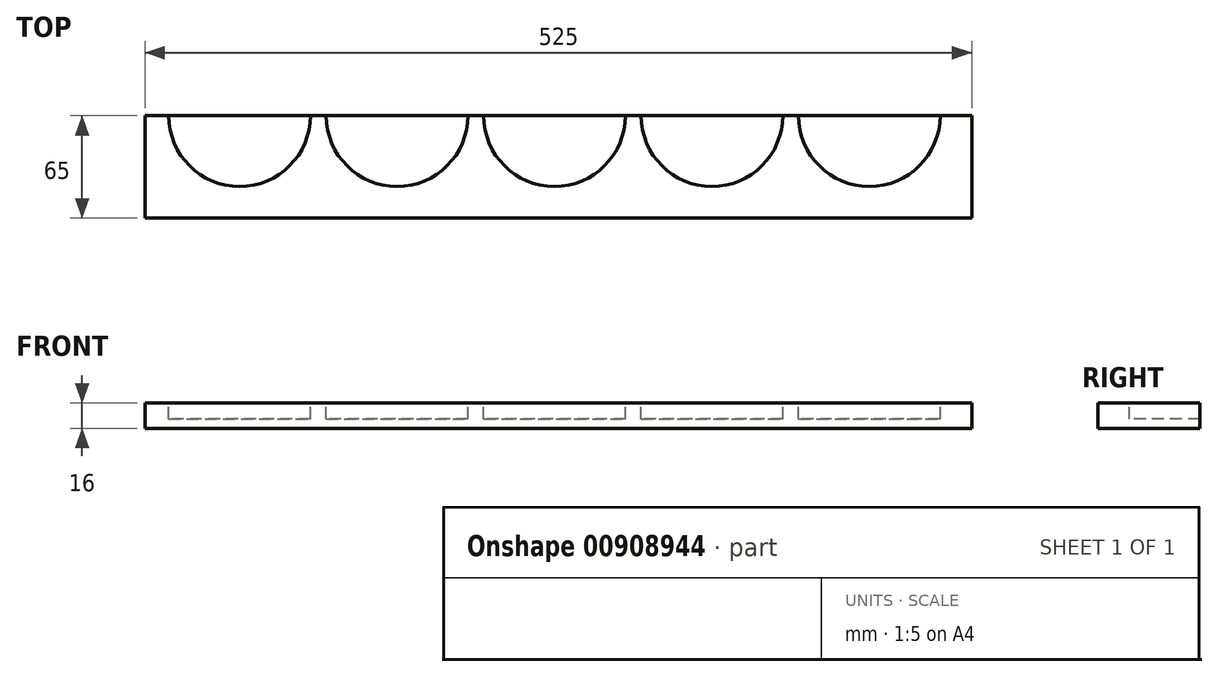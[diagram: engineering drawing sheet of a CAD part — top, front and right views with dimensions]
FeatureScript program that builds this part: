
annotation { "Feature Type Name" : "Feature", "Feature Type Description" : "" }
export const myFeature = defineFeature(function(context is Context, id is Id, definition is map)
    precondition{}
    {
        {
            var Q0;
            Q0=qCreatedBy(makeId("Front.planeOp"),FACE);
            var sketch = newSketch(context, id + "F0", { "sketchPlane" : qUnion([Q0])});
            skLineSegment(sketch, "E0.bottom", {"start": v(262.5, 8) * mm, "end": v(-262.5, 8) * mm});
            skLineSegment(sketch, "E0.top", {"start": v(262.5, -8) * mm, "end": v(-262.5, -8) * mm});
            skLineSegment(sketch, "E0.left", {"start": v(262.5, 8) * mm, "end": v(262.5, -8) * mm});
            skLineSegment(sketch, "E0.right", {"start": v(-262.5, 8) * mm, "end": v(-262.5, -8) * mm});
            skPoint(sketch, "E0.middle", {"position": v(0, 0) * mm});
            skSolve(sketch);
        }
        {
            var Q0;
            Q0=makeQuery(id+"F0.imprint","IMPRINT",FACE,{"disambiguationData":[TD([[makeQuery(id+"F0.imprint","IMPRINT",EDGE,{"derivedFrom":sQuery(id+"F0.wireOp",EDGE,"E0.bottom")}),1.0]])]});
            extrude(context, id + "F1", {"entities" : qUnion([Q0]), "oppositeDirection" : true, "depth" : 65 * mm, "offsetDistance" : 25 * mm});
        }
        {
            var Q0;
            Q0=makeQuery(id+"F1.opExtrude","SWEPT_FACE",FACE,{"disambiguationData":[OSD([sQuery(id+"F0.wireOp",EDGE,"E0.bottom")])]});
            var sketch = newSketch(context, id + "F2", { "sketchPlane" : qUnion([Q0])});
            skLineSegment(sketch, "E1", {"start": v(-262.5, 0) * mm, "end": v(-262.5, 65) * mm});
            skArc(sketch, "E2", {"start": v(-247.5, 65) * mm, "mid": v(-202.5, 20) * mm, "end": v(-157.5, 65) * mm});
            skArc(sketch, "E3.1.0.0", {"start": v(-147.5, 65) * mm, "mid": v(-102.5, 20) * mm, "end": v(-57.5, 65) * mm});
            skArc(sketch, "E3.2.0.0", {"start": v(-47.5, 65) * mm, "mid": v(-2.5, 20) * mm, "end": v(42.5, 65) * mm});
            skArc(sketch, "E3.3.0.0", {"start": v(52.5, 65) * mm, "mid": v(97.5, 20) * mm, "end": v(142.5, 65) * mm});
            skArc(sketch, "E3.4.0.0", {"start": v(152.5, 65) * mm, "mid": v(197.5, 20) * mm, "end": v(242.5, 65) * mm});
            skLineSegment(sketch, "E3.direction1", {"start": v(-247.5, 65) * mm, "end": v(-147.5, 65) * mm, "construction": true});
            skSolve(sketch);
        }
        {
            var Q0;
            {var subQ0=sQuery(id+"F2.wireOp",EDGE,"E2");Q0=makeQuery(id+"F2.imprint","IMPRINT",FACE,{"disambiguationData":[TD([[makeQuery(id+"F2.imprint","IMPRINT",EDGE,{"derivedFrom":subQ0}),1.0]])]});}
            var Q1;
            {var subQ0=sQuery(id+"F2.wireOp",EDGE,"E3.1.0.0");Q1=makeQuery(id+"F2.imprint","IMPRINT",FACE,{"disambiguationData":[TD([[makeQuery(id+"F2.imprint","IMPRINT",EDGE,{"derivedFrom":subQ0}),1.0]])]});}
            var Q2;
            {var subQ0=sQuery(id+"F2.wireOp",EDGE,"E3.2.0.0");Q2=makeQuery(id+"F2.imprint","IMPRINT",FACE,{"disambiguationData":[TD([[makeQuery(id+"F2.imprint","IMPRINT",EDGE,{"derivedFrom":subQ0}),1.0]])]});}
            var Q3;
            {var subQ0=sQuery(id+"F2.wireOp",EDGE,"E3.3.0.0");Q3=makeQuery(id+"F2.imprint","IMPRINT",FACE,{"disambiguationData":[TD([[makeQuery(id+"F2.imprint","IMPRINT",EDGE,{"derivedFrom":subQ0}),1.0]])]});}
            var Q4;
            {var subQ0=sQuery(id+"F2.wireOp",EDGE,"E3.4.0.0");Q4=makeQuery(id+"F2.imprint","IMPRINT",FACE,{"disambiguationData":[TD([[makeQuery(id+"F2.imprint","IMPRINT",EDGE,{"derivedFrom":subQ0}),1.0]])]});}
            extrude(context, id + "F3", {"entities" : qUnion([Q0, Q1, Q2, Q3, Q4]), "operationType" : NewBodyOperationType.REMOVE, "oppositeDirection" : true, "depth" : 10 * mm, "offsetDistance" : 25 * mm});
        }
    });
